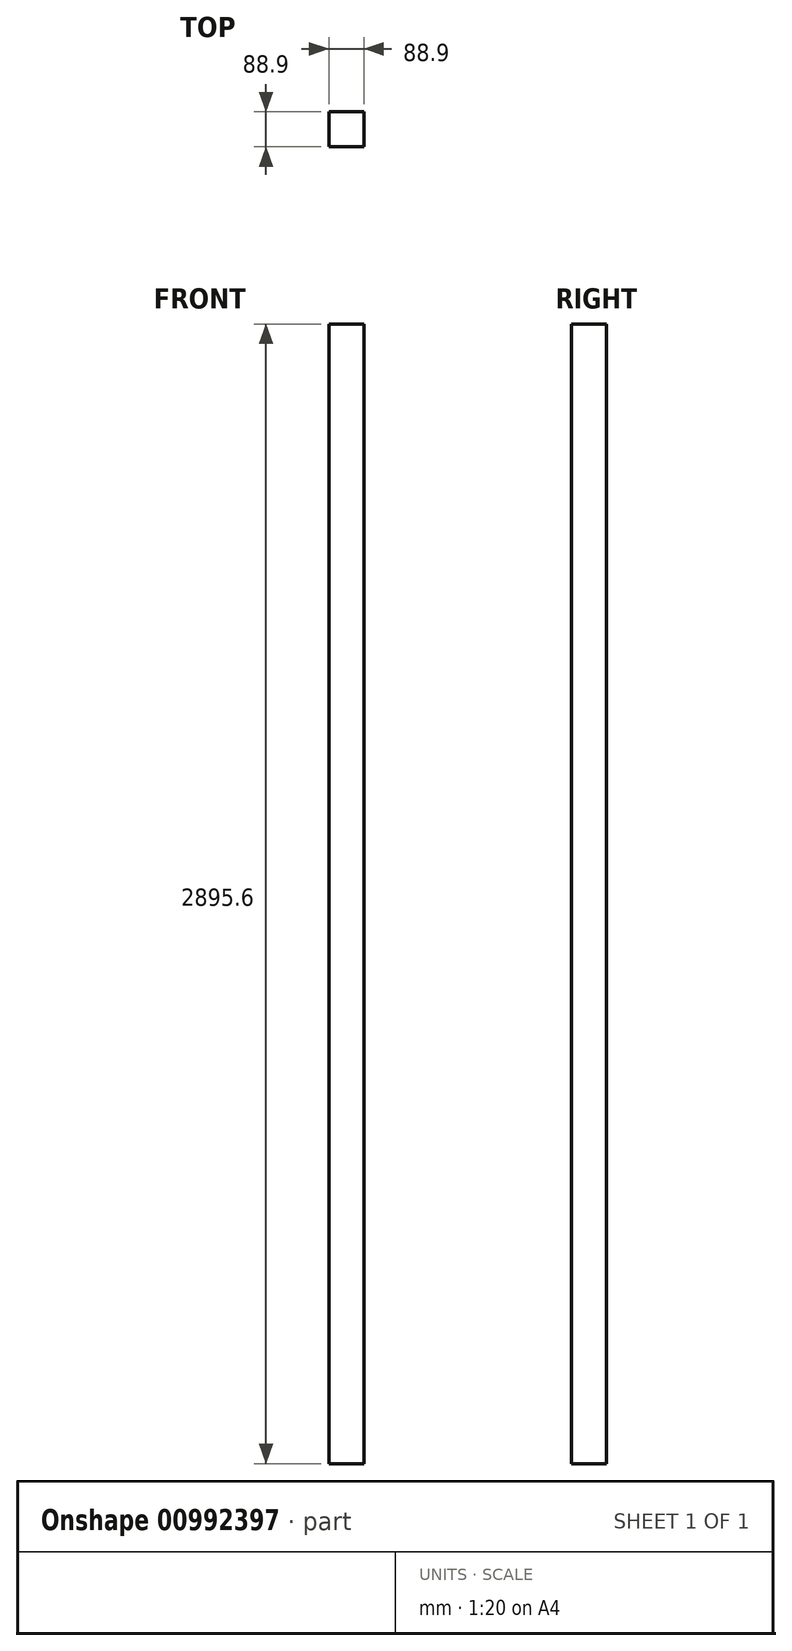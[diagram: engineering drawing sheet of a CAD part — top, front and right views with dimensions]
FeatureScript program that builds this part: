
annotation { "Feature Type Name" : "Feature", "Feature Type Description" : "" }
export const myFeature = defineFeature(function(context is Context, id is Id, definition is map)
    precondition{}
    {
        {
            var Q0;
            Q0=qCreatedBy(makeId("Top.planeOp"),FACE);
            var sketch = newSketch(context, id + "F0", { "sketchPlane" : qUnion([Q0])});
            skLineSegment(sketch, "E0.bottom", {"start": v(44.45, 44.45) * mm, "end": v(-44.45, 44.45) * mm});
            skLineSegment(sketch, "E0.top", {"start": v(44.45, -44.45) * mm, "end": v(-44.45, -44.45) * mm});
            skLineSegment(sketch, "E0.left", {"start": v(44.45, 44.45) * mm, "end": v(44.45, -44.45) * mm});
            skLineSegment(sketch, "E0.right", {"start": v(-44.45, 44.45) * mm, "end": v(-44.45, -44.45) * mm});
            skPoint(sketch, "E0.middle", {"position": v(0, 0) * mm});
            skSolve(sketch);
        }
        {
            var Q0;
            Q0 = qSketchRegion(id + "F0", true);
            extrude(context, id + "F1", {"entities" : qUnion([Q0]), "depth" : 2286 * mm, "offsetDistance" : 25.4 * mm, "hasSecondDirection" : true, "secondDirectionOppositeDirection" : true, "secondDirectionDepth" : 609.6 * mm});
        }
    });
